# Revit family: Curtain Track_Metlam_L Bend
name_source: partatom
category: Specialty Equipment
revit_build: Autodesk Revit 2016 (Build: 20161004_0715(x64)
units: mm (PartAtom-declared; Revit-internal decimal feet)

## family parameters
Always vertical = Yes
Cut with Voids When Loaded = No
OmniClass Number = 23.40.20.21.44
OmniClass Title = Shower Rods, Curtains
Part Type = Normal
Room Calculation Point = Yes
Round Connector Dimension = Use Diameter
Shared = No
Work Plane-Based = No

## types (1)
- 300h (ML-SCT-SERIES-L)
    Curtain_Option = Yes
    Description = L Bend Shower Curtain Track System
    Fabric_Material = z_Metlam_White
    Manufacturer = Metlam
    Manufacturer_Overall Height = 300 mm
    Manufacturer_Spec Code = ML-SCT-SERIES-L
    Manufacturer_URL__Product Specific = https://www.metlam.com.au
    Material_ANZRS = z_Metlam_Metal_Stainless Steel_Satin
    Model = ML-SCT-SERIES-L
    Type Comments = Grab Rails
    URL = http://www.metlam.com.au

## geometry (parser evidence)
native form markers: Sweep x2
no freeform markers — native parametric forms only
